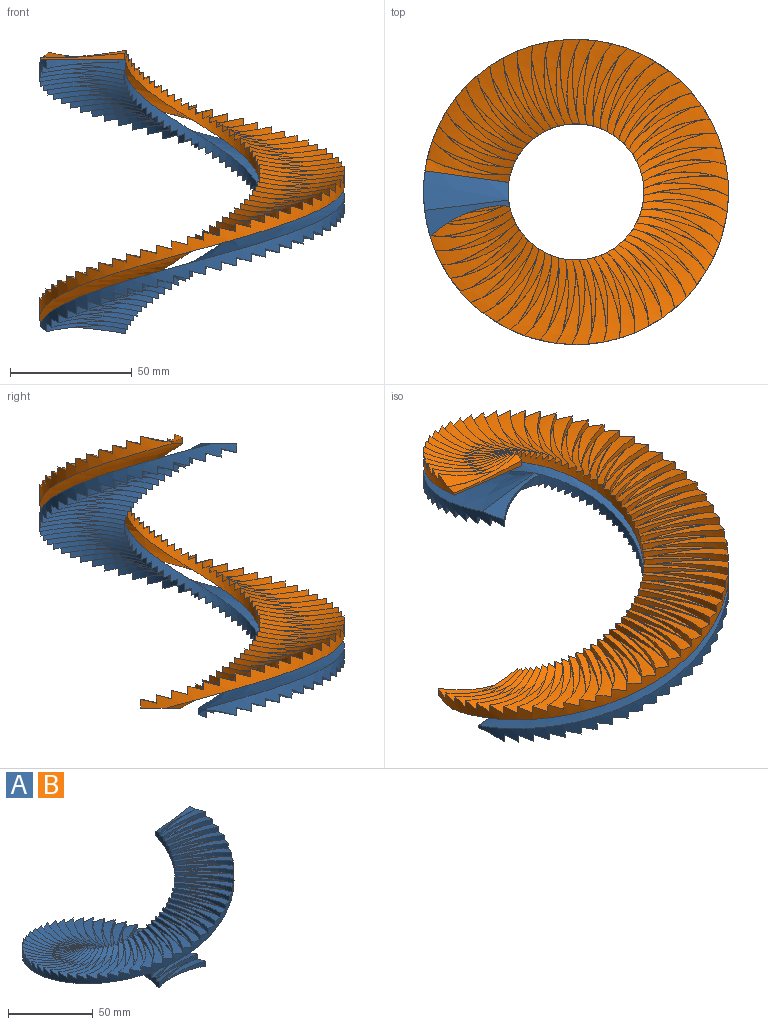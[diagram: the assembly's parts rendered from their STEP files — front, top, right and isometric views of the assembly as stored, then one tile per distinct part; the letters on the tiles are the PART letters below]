
ASSEMBLY  parts=2 mates=1
PART A: 249 faces, bbox 134.5x134.5x124.1 mm
  f0: cylinder r=27.93mm len=112.5mm, axis (0,0,-1), area 831.8mm2, adj f2,f3,f4,f5,f6,f7,f8,f9
  f1: cylinder r=62.62mm len=125.24mm, axis (0,0,-1), area 1964.2mm2, adj f2,f3,f4,f126,f127,f128,f129,f130
  f2: plane 34.97x10.85mm, normal (0,0,-1), area 146.9mm2, adj f0,f1,f125,f247,f248
  f3: plane 34.2x5.86mm, normal (-0.17,0.99,0), area 50.9mm2, adj f0,f1,f4,f248
  f4: bspline ~40.21x16.63mm, area 94.5mm2, adj f0,f1,f3,f5,f126
  f5: bspline ~39.85x15.98mm, area 49.6mm2, adj f0,f4,f6,f126
  f6: bspline ~38.72x13.77mm, area 65.8mm2, adj f0,f5,f7,f126,f127
  f7: bspline ~37.98x15.95mm, area 41.2mm2, adj f0,f6,f8,f127,f128,f129
  f8: bspline ~39.79x14.14mm, area 55mm2, adj f0,f7,f9,f129
  f9: bspline ~37.93x15.94mm, area 41.3mm2, adj f0,f8,f10,f129,f130,f131
  f10: bspline ~40.42x16.75mm, area 66.7mm2, adj f0,f9,f11,f131
  f11: bspline ~37.46x15.96mm, area 41.2mm2, adj f0,f10,f12,f131,f132,f133
  f12: bspline ~40.61x19.84mm, area 66.8mm2, adj f0,f11,f13,f133
  f13: bspline ~36.57x15.97mm, area 41.2mm2, adj f0,f12,f14,f133,f134,f135
  f14: bspline ~40.36x23.15mm, area 54.7mm2, adj f0,f13,f15,f135
  f15: bspline ~35.31x15.95mm, area 41.2mm2, adj f0,f14,f16,f135,f136,f137
  f16: bspline ~39.67x26.21mm, area 66.4mm2, adj f0,f15,f17,f137
  f17: bspline ~33.65x17.74mm, area 41.3mm2, adj f0,f16,f18,f137,f138,f139
  f18: bspline ~38.53x28.98mm, area 66.8mm2, adj f0,f17,f19,f139
  f19: bspline ~31.59x21.16mm, area 41.2mm2, adj f0,f18,f20,f139,f140,f141
  f20: bspline ~36.98x31.43mm, area 66.5mm2, adj f0,f19,f21,f141
  f21: bspline ~29.21x24.34mm, area 41.2mm2, adj f0,f20,f22,f141,f142,f143
  f22: bspline ~35.03x33.54mm, area 54.8mm2, adj f0,f21,f23,f143
  f23: bspline ~27.26x26.55mm, area 41.2mm2, adj f0,f22,f24,f143,f144,f145
  f24: bspline ~35.28x32.68mm, area 66.5mm2, adj f0,f23,f25,f145
  f25: bspline ~29.88x23.55mm, area 41.3mm2, adj f0,f24,f26,f145,f146,f147
  f26: bspline ~36.63x29.97mm, area 66.9mm2, adj f0,f25,f27,f147
  f27: bspline ~32.17x20.27mm, area 41.2mm2, adj f0,f26,f28,f147,f148,f149
  f28: bspline ~37.58x26.95mm, area 54.9mm2, adj f0,f27,f29,f149
  f29: bspline ~34.11x16.81mm, area 41.2mm2, adj f0,f28,f30,f149,f150,f151
  f30: bspline ~38.12x23.63mm, area 54.9mm2, adj f0,f29,f31,f151
  f31: bspline ~35.67x15.94mm, area 41.3mm2, adj f0,f30,f32,f151,f152,f153
  f32: bspline ~38.25x20.05mm, area 66.6mm2, adj f0,f31,f33,f153
  f33: bspline ~36.84x15.95mm, area 41.3mm2, adj f0,f32,f34,f153,f154,f155
  f34: bspline ~37.95x16.63mm, area 67.1mm2, adj f0,f33,f35,f155
  f35: bspline ~37.61x15.98mm, area 41.2mm2, adj f0,f34,f36,f155,f156
  f36: bspline ~38.72x13.77mm, area 65.8mm2, adj f0,f35,f37,f156,f157
  f37: bspline ~37.98x15.95mm, area 41.2mm2, adj f0,f36,f38,f157,f158,f159
  f38: bspline ~39.79x14.14mm, area 55mm2, adj f0,f37,f39,f159
  f39: bspline ~37.93x15.94mm, area 41.3mm2, adj f0,f38,f40,f159,f160,f161
  f40: bspline ~40.42x16.75mm, area 66.7mm2, adj f0,f39,f41,f161
  f41: bspline ~37.46x15.96mm, area 41.2mm2, adj f0,f40,f42,f161,f162,f163
  f42: bspline ~40.61x19.84mm, area 66.8mm2, adj f0,f41,f43,f163
  f43: bspline ~36.57x15.97mm, area 41.2mm2, adj f0,f42,f44,f163,f164,f165
  f44: bspline ~40.36x23.15mm, area 54.7mm2, adj f0,f43,f45,f165
  f45: bspline ~35.31x15.95mm, area 41.2mm2, adj f0,f44,f46,f165,f166,f167
  f46: bspline ~39.67x26.21mm, area 66.4mm2, adj f0,f45,f47,f167
  f47: bspline ~33.65x17.74mm, area 41.3mm2, adj f0,f46,f48,f167,f168,f169
  f48: bspline ~38.53x28.98mm, area 66.8mm2, adj f0,f47,f49,f169
  f49: bspline ~31.59x21.16mm, area 41.2mm2, adj f0,f48,f50,f169,f170,f171
  f50: bspline ~36.98x31.43mm, area 66.5mm2, adj f0,f49,f51,f171
  f51: bspline ~29.21x24.34mm, area 41.2mm2, adj f0,f50,f52,f171,f172,f173
  f52: bspline ~35.03x33.54mm, area 54.8mm2, adj f0,f51,f53,f173
  f53: bspline ~27.26x26.55mm, area 41.2mm2, adj f0,f52,f54,f173,f174,f175
  f54: bspline ~35.28x32.68mm, area 66.5mm2, adj f0,f53,f55,f175
  f55: bspline ~29.88x23.55mm, area 41.3mm2, adj f0,f54,f56,f175,f176,f177
  f56: bspline ~36.63x29.97mm, area 66.9mm2, adj f0,f55,f57,f177
  f57: bspline ~32.17x20.27mm, area 41.2mm2, adj f0,f56,f58,f177,f178,f179
  f58: bspline ~37.58x26.95mm, area 54.9mm2, adj f0,f57,f59,f179
  f59: bspline ~34.11x16.81mm, area 41.2mm2, adj f0,f58,f60,f179,f180,f181
  f60: bspline ~38.12x23.63mm, area 54.9mm2, adj f0,f59,f61,f181
  f61: bspline ~35.67x15.94mm, area 41.3mm2, adj f0,f60,f62,f181,f182,f183
  f62: bspline ~38.25x20.05mm, area 66.6mm2, adj f0,f61,f63,f183
  f63: bspline ~36.84x15.95mm, area 41.3mm2, adj f0,f62,f64,f183,f184,f185
  f64: bspline ~37.95x16.63mm, area 67.1mm2, adj f0,f63,f65,f185
  f65: bspline ~37.61x15.98mm, area 41.2mm2, adj f0,f64,f66,f185,f186
  f66: bspline ~38.72x13.77mm, area 65.8mm2, adj f0,f65,f67,f186,f187
  f67: bspline ~37.98x15.95mm, area 41.2mm2, adj f0,f66,f68,f187,f188,f189
  f68: bspline ~39.79x14.14mm, area 55mm2, adj f0,f67,f69,f189
  f69: bspline ~37.93x15.94mm, area 41.3mm2, adj f0,f68,f70,f189,f190,f191
  f70: bspline ~40.42x16.75mm, area 66.7mm2, adj f0,f69,f71,f191
  f71: bspline ~37.46x15.96mm, area 41.2mm2, adj f0,f70,f72,f191,f192,f193
  f72: bspline ~40.61x19.84mm, area 66.8mm2, adj f0,f71,f73,f193
  f73: bspline ~36.57x15.97mm, area 41.2mm2, adj f0,f72,f74,f193,f194,f195
  f74: bspline ~40.36x23.15mm, area 54.7mm2, adj f0,f73,f75,f195
  f75: bspline ~35.31x15.95mm, area 41.2mm2, adj f0,f74,f76,f195,f196,f197
  f76: bspline ~39.67x26.21mm, area 66.4mm2, adj f0,f75,f77,f197
  f77: bspline ~33.65x17.74mm, area 41.3mm2, adj f0,f76,f78,f197,f198,f199
  f78: bspline ~38.53x28.98mm, area 66.8mm2, adj f0,f77,f79,f199
  f79: bspline ~31.59x21.16mm, area 41.2mm2, adj f0,f78,f80,f199,f200,f201
  f80: bspline ~36.98x31.43mm, area 66.5mm2, adj f0,f79,f81,f201
  f81: bspline ~29.21x24.34mm, area 41.2mm2, adj f0,f80,f82,f201,f202,f203
  f82: bspline ~35.03x33.54mm, area 54.8mm2, adj f0,f81,f83,f203
  f83: bspline ~27.26x26.55mm, area 41.2mm2, adj f0,f82,f84,f203,f204,f205
  f84: bspline ~35.28x32.68mm, area 66.5mm2, adj f0,f83,f85,f205
  f85: bspline ~29.88x23.55mm, area 41.3mm2, adj f0,f84,f86,f205,f206,f207
  f86: bspline ~36.63x29.97mm, area 66.9mm2, adj f0,f85,f87,f207
  f87: bspline ~32.17x20.27mm, area 41.2mm2, adj f0,f86,f88,f207,f208,f209
  f88: bspline ~37.58x26.95mm, area 54.9mm2, adj f0,f87,f89,f209
  f89: bspline ~34.11x16.81mm, area 41.2mm2, adj f0,f88,f90,f209,f210,f211
  f90: bspline ~38.12x23.63mm, area 54.9mm2, adj f0,f89,f91,f211
  f91: bspline ~35.67x15.94mm, area 41.3mm2, adj f0,f90,f92,f211,f212,f213
  f92: bspline ~38.25x20.05mm, area 66.6mm2, adj f0,f91,f93,f213
  f93: bspline ~36.84x15.95mm, area 41.3mm2, adj f0,f92,f94,f213,f214,f215
  f94: bspline ~37.95x16.63mm, area 67.1mm2, adj f0,f93,f95,f215
  f95: bspline ~37.61x15.98mm, area 41.2mm2, adj f0,f94,f96,f215,f216
  f96: bspline ~38.72x13.77mm, area 65.8mm2, adj f0,f95,f97,f216,f217
  f97: bspline ~37.98x15.95mm, area 41.2mm2, adj f0,f96,f98,f217,f218,f219
  f98: bspline ~39.79x14.14mm, area 55mm2, adj f0,f97,f99,f219
  f99: bspline ~37.93x15.94mm, area 41.3mm2, adj f0,f98,f100,f219,f220,f221
  f100: bspline ~40.42x16.75mm, area 66.7mm2, adj f0,f99,f101,f221
  f101: bspline ~37.46x15.96mm, area 41.2mm2, adj f0,f100,f102,f221,f222,f223
  f102: bspline ~40.61x19.84mm, area 66.8mm2, adj f0,f101,f103,f223
  f103: bspline ~36.57x15.97mm, area 41.2mm2, adj f0,f102,f104,f223,f224,f225
  f104: bspline ~40.36x23.15mm, area 54.7mm2, adj f0,f103,f105,f225
  f105: bspline ~35.31x15.95mm, area 41.2mm2, adj f0,f104,f106,f225,f226,f227
  f106: bspline ~39.67x26.21mm, area 66.4mm2, adj f0,f105,f107,f227
  f107: bspline ~33.65x17.74mm, area 41.3mm2, adj f0,f106,f108,f227,f228,f229
  f108: bspline ~38.53x28.98mm, area 66.8mm2, adj f0,f107,f109,f229
  f109: bspline ~31.59x21.16mm, area 41.2mm2, adj f0,f108,f110,f229,f230,f231
  f110: bspline ~36.98x31.43mm, area 66.5mm2, adj f0,f109,f111,f231
  f111: bspline ~29.21x24.34mm, area 41.2mm2, adj f0,f110,f112,f231,f232,f233
  f112: bspline ~35.03x33.54mm, area 54.8mm2, adj f0,f111,f113,f233
  f113: bspline ~27.26x26.55mm, area 41.2mm2, adj f0,f112,f114,f233,f234,f235
  f114: bspline ~35.28x32.68mm, area 66.5mm2, adj f0,f113,f115,f235
  f115: bspline ~29.88x23.55mm, area 41.3mm2, adj f0,f114,f116,f235,f236,f237
  f116: bspline ~36.63x29.97mm, area 66.9mm2, adj f0,f115,f117,f237
  f117: bspline ~32.17x20.27mm, area 41.2mm2, adj f0,f116,f118,f237,f238,f239
  f118: bspline ~37.58x26.95mm, area 54.9mm2, adj f0,f117,f119,f239
  f119: bspline ~34.11x16.81mm, area 41.2mm2, adj f0,f118,f120,f239,f240,f241
  f120: bspline ~38.12x23.63mm, area 54.9mm2, adj f0,f119,f121,f241
  f121: bspline ~35.67x15.94mm, area 41.3mm2, adj f0,f120,f122,f241,f242,f243
  f122: bspline ~38.25x20.05mm, area 66.6mm2, adj f0,f121,f123,f243
  f123: bspline ~36.84x15.95mm, area 41.3mm2, adj f0,f122,f124,f243,f244,f245
  f124: bspline ~37.95x16.63mm, area 67.1mm2, adj f0,f123,f125,f245
  f125: bspline ~37.61x15.98mm, area 45.3mm2, adj f0,f2,f124,f245,f246,f247
  f126: bspline ~40.03x16.78mm, area 102.9mm2, adj f1,f4,f5,f6,f127
  f127: bspline ~39.98x15.05mm, area 56.2mm2, adj f1,f6,f7,f126,f128
  f128: bspline ~40.44x19.89mm, area 99.9mm2, adj f1,f7,f127,f129
  f129: bspline ~39.32x15.01mm, area 56.8mm2, adj f1,f7,f8,f9,f128,f130
  f130: bspline ~40.41x23.19mm, area 100mm2, adj f1,f9,f129,f131
  f131: bspline ~38.23x15mm, area 57.4mm2, adj f1,f9,f10,f11,f130,f132
  f132: bspline ~39.93x26.81mm, area 100mm2, adj f1,f11,f131,f133
  f133: bspline ~36.72x16.47mm, area 57.3mm2, adj f1,f11,f12,f13,f132,f134
  f134: bspline ~39.02x30.13mm, area 100.1mm2, adj f1,f13,f133,f135
  f135: bspline ~34.79x20.18mm, area 56.3mm2, adj f1,f13,f14,f15,f134,f136
  f136: bspline ~37.67x33.14mm, area 99.9mm2, adj f1,f15,f135,f137
  f137: bspline ~32.52x23.76mm, area 57mm2, adj f1,f15,f16,f17,f136,f138
  f138: bspline ~35.92x35.78mm, area 100mm2, adj f1,f17,f137,f139
  f139: bspline ~29.87x27.02mm, area 57.6mm2, adj f1,f17,f18,f19,f138,f140
  f140: bspline ~38.02x33.77mm, area 100.1mm2, adj f1,f19,f139,f141
  f141: bspline ~29.95x26.88mm, area 56.8mm2, adj f1,f19,f20,f21,f140,f142
  f142: bspline ~39.85x31.25mm, area 100mm2, adj f1,f21,f141,f143
  f143: bspline ~32.59x23.6mm, area 56.5mm2, adj f1,f21,f22,f23,f142,f144
  f144: bspline ~41.24x28.39mm, area 99.9mm2, adj f1,f23,f143,f145
  f145: bspline ~34.9x20.1mm, area 57.1mm2, adj f1,f23,f24,f25,f144,f146
  f146: bspline ~42.18x25.22mm, area 100mm2, adj f1,f25,f145,f147
  f147: bspline ~36.8x16.35mm, area 57.8mm2, adj f1,f25,f26,f27,f146,f148
  f148: bspline ~42.66x21.89mm, area 100.1mm2, adj f1,f27,f147,f149
  f149: bspline ~38.27x15.04mm, area 56.4mm2, adj f1,f27,f28,f29,f148,f150
  f150: bspline ~42.67x18.91mm, area 100mm2, adj f1,f29,f149,f151
  f151: bspline ~39.36x15.02mm, area 56.7mm2, adj f1,f29,f30,f31,f150,f152
  f152: bspline ~42.21x16.28mm, area 100mm2, adj f1,f31,f151,f153
  f153: bspline ~40.01x15mm, area 57.3mm2, adj f1,f31,f32,f33,f152,f154
  f154: bspline ~41.29x14.24mm, area 100mm2, adj f1,f33,f153,f155
  f155: bspline ~40.21x15.01mm, area 57.9mm2, adj f1,f33,f34,f35,f154,f156
  f156: bspline ~40.03x16.78mm, area 100.5mm2, adj f1,f35,f36,f155,f157
  f157: bspline ~39.98x15.05mm, area 56.2mm2, adj f1,f36,f37,f156,f158
  f158: bspline ~40.44x19.89mm, area 99.9mm2, adj f1,f37,f157,f159
  f159: bspline ~39.32x15.01mm, area 56.8mm2, adj f1,f37,f38,f39,f158,f160
  f160: bspline ~40.41x23.19mm, area 100mm2, adj f1,f39,f159,f161
  f161: bspline ~38.23x15mm, area 57.4mm2, adj f1,f39,f40,f41,f160,f162
  f162: bspline ~39.93x26.81mm, area 100mm2, adj f1,f41,f161,f163
  f163: bspline ~36.72x16.47mm, area 57.3mm2, adj f1,f41,f42,f43,f162,f164
  f164: bspline ~39.02x30.13mm, area 100.1mm2, adj f1,f43,f163,f165
  f165: bspline ~34.79x20.18mm, area 56.3mm2, adj f1,f43,f44,f45,f164,f166
  f166: bspline ~37.67x33.14mm, area 99.9mm2, adj f1,f45,f165,f167
  f167: bspline ~32.52x23.76mm, area 57mm2, adj f1,f45,f46,f47,f166,f168
  f168: bspline ~35.92x35.78mm, area 100mm2, adj f1,f47,f167,f169
  f169: bspline ~29.87x27.02mm, area 57.6mm2, adj f1,f47,f48,f49,f168,f170
  f170: bspline ~38.02x33.77mm, area 100.1mm2, adj f1,f49,f169,f171
  f171: bspline ~29.95x26.88mm, area 56.8mm2, adj f1,f49,f50,f51,f170,f172
  f172: bspline ~39.85x31.25mm, area 100mm2, adj f1,f51,f171,f173
  f173: bspline ~32.59x23.6mm, area 56.5mm2, adj f1,f51,f52,f53,f172,f174
  f174: bspline ~41.24x28.39mm, area 99.9mm2, adj f1,f53,f173,f175
  f175: bspline ~34.9x20.1mm, area 57.1mm2, adj f1,f53,f54,f55,f174,f176
  f176: bspline ~42.18x25.22mm, area 100mm2, adj f1,f55,f175,f177
  f177: bspline ~36.8x16.35mm, area 57.8mm2, adj f1,f55,f56,f57,f176,f178
  f178: bspline ~42.66x21.89mm, area 100.1mm2, adj f1,f57,f177,f179
  f179: bspline ~38.27x15.04mm, area 56.4mm2, adj f1,f57,f58,f59,f178,f180
  f180: bspline ~42.67x18.91mm, area 100mm2, adj f1,f59,f179,f181
  f181: bspline ~39.36x15.02mm, area 56.7mm2, adj f1,f59,f60,f61,f180,f182
  f182: bspline ~42.21x16.28mm, area 100mm2, adj f1,f61,f181,f183
  f183: bspline ~40.01x15mm, area 57.3mm2, adj f1,f61,f62,f63,f182,f184
  f184: bspline ~41.29x14.24mm, area 100mm2, adj f1,f63,f183,f185
  f185: bspline ~40.21x15.01mm, area 57.9mm2, adj f1,f63,f64,f65,f184,f186
  f186: bspline ~40.03x16.78mm, area 100.5mm2, adj f1,f65,f66,f185,f187
  f187: bspline ~39.98x15.05mm, area 56.2mm2, adj f1,f66,f67,f186,f188
  f188: bspline ~40.44x19.89mm, area 99.9mm2, adj f1,f67,f187,f189
  f189: bspline ~39.32x15.01mm, area 56.8mm2, adj f1,f67,f68,f69,f188,f190
  f190: bspline ~40.41x23.19mm, area 100mm2, adj f1,f69,f189,f191
  f191: bspline ~38.23x15mm, area 57.4mm2, adj f1,f69,f70,f71,f190,f192
  f192: bspline ~39.93x26.81mm, area 100mm2, adj f1,f71,f191,f193
  f193: bspline ~36.72x16.47mm, area 57.3mm2, adj f1,f71,f72,f73,f192,f194
  f194: bspline ~39.02x30.13mm, area 100.1mm2, adj f1,f73,f193,f195
  f195: bspline ~34.79x20.18mm, area 56.3mm2, adj f1,f73,f74,f75,f194,f196
  f196: bspline ~37.67x33.14mm, area 99.9mm2, adj f1,f75,f195,f197
  f197: bspline ~32.52x23.76mm, area 57mm2, adj f1,f75,f76,f77,f196,f198
  f198: bspline ~35.92x35.78mm, area 100mm2, adj f1,f77,f197,f199
  f199: bspline ~29.87x27.02mm, area 57.6mm2, adj f1,f77,f78,f79,f198,f200
  f200: bspline ~38.02x33.77mm, area 100.1mm2, adj f1,f79,f199,f201
  f201: bspline ~29.95x26.88mm, area 56.8mm2, adj f1,f79,f80,f81,f200,f202
  f202: bspline ~39.85x31.25mm, area 100mm2, adj f1,f81,f201,f203
  f203: bspline ~32.59x23.6mm, area 56.5mm2, adj f1,f81,f82,f83,f202,f204
  f204: bspline ~41.24x28.39mm, area 99.9mm2, adj f1,f83,f203,f205
  f205: bspline ~34.9x20.1mm, area 57.1mm2, adj f1,f83,f84,f85,f204,f206
  f206: bspline ~42.18x25.22mm, area 100mm2, adj f1,f85,f205,f207
  f207: bspline ~36.8x16.35mm, area 57.8mm2, adj f1,f85,f86,f87,f206,f208
  f208: bspline ~42.66x21.89mm, area 100.1mm2, adj f1,f87,f207,f209
  f209: bspline ~38.27x15.04mm, area 56.4mm2, adj f1,f87,f88,f89,f208,f210
  f210: bspline ~42.67x18.91mm, area 100mm2, adj f1,f89,f209,f211
  f211: bspline ~39.36x15.02mm, area 56.7mm2, adj f1,f89,f90,f91,f210,f212
  f212: bspline ~42.21x16.28mm, area 100mm2, adj f1,f91,f211,f213
  f213: bspline ~40.01x15mm, area 57.3mm2, adj f1,f91,f92,f93,f212,f214
  f214: bspline ~41.29x14.24mm, area 100mm2, adj f1,f93,f213,f215
  f215: bspline ~40.21x15.01mm, area 57.9mm2, adj f1,f93,f94,f95,f214,f216
  f216: bspline ~40.03x16.78mm, area 100.5mm2, adj f1,f95,f96,f215,f217
  f217: bspline ~39.98x15.05mm, area 56.2mm2, adj f1,f96,f97,f216,f218
  f218: bspline ~40.44x19.89mm, area 99.9mm2, adj f1,f97,f217,f219
  f219: bspline ~39.32x15.01mm, area 56.8mm2, adj f1,f97,f98,f99,f218,f220
  f220: bspline ~40.41x23.19mm, area 100mm2, adj f1,f99,f219,f221
  f221: bspline ~38.23x15mm, area 57.4mm2, adj f1,f99,f100,f101,f220,f222
  f222: bspline ~39.93x26.81mm, area 100mm2, adj f1,f101,f221,f223
  f223: bspline ~36.72x16.47mm, area 57.3mm2, adj f1,f101,f102,f103,f222,f224
  f224: bspline ~39.02x30.13mm, area 100.1mm2, adj f1,f103,f223,f225
  f225: bspline ~34.79x20.18mm, area 56.3mm2, adj f1,f103,f104,f105,f224,f226
  f226: bspline ~37.67x33.14mm, area 99.9mm2, adj f1,f105,f225,f227
  f227: bspline ~32.52x23.76mm, area 57mm2, adj f1,f105,f106,f107,f226,f228
  f228: bspline ~35.92x35.78mm, area 100mm2, adj f1,f107,f227,f229
  f229: bspline ~29.87x27.02mm, area 57.6mm2, adj f1,f107,f108,f109,f228,f230
  f230: bspline ~38.02x33.77mm, area 100.1mm2, adj f1,f109,f229,f231
  f231: bspline ~29.95x26.88mm, area 56.8mm2, adj f1,f109,f110,f111,f230,f232
  f232: bspline ~39.85x31.25mm, area 100mm2, adj f1,f111,f231,f233
  f233: bspline ~32.59x23.6mm, area 56.5mm2, adj f1,f111,f112,f113,f232,f234
  f234: bspline ~41.24x28.39mm, area 99.9mm2, adj f1,f113,f233,f235
  f235: bspline ~34.9x20.1mm, area 57.1mm2, adj f1,f113,f114,f115,f234,f236
  f236: bspline ~42.18x25.22mm, area 100mm2, adj f1,f115,f235,f237
  f237: bspline ~36.8x16.35mm, area 57.8mm2, adj f1,f115,f116,f117,f236,f238
  f238: bspline ~42.66x21.89mm, area 100.1mm2, adj f1,f117,f237,f239
  f239: bspline ~38.27x15.04mm, area 56.4mm2, adj f1,f117,f118,f119,f238,f240
  f240: bspline ~42.67x18.91mm, area 100mm2, adj f1,f119,f239,f241
  f241: bspline ~39.36x15.02mm, area 56.7mm2, adj f1,f119,f120,f121,f240,f242
  f242: bspline ~42.21x16.28mm, area 100mm2, adj f1,f121,f241,f243
  f243: bspline ~40.01x15mm, area 57.3mm2, adj f1,f121,f122,f123,f242,f244
  f244: bspline ~41.29x14.24mm, area 100mm2, adj f1,f123,f243,f245
  f245: bspline ~40.21x15.01mm, area 57.9mm2, adj f1,f123,f124,f125,f244,f246
  f246: bspline ~40.03x16.78mm, area 100.1mm2, adj f1,f125,f245,f247
  f247: bspline ~39.98x15.05mm, area 61.2mm2, adj f1,f2,f125,f246
  f248: bspline ~134.46x134.46mm, area 10637.6mm2, adj f0,f1,f2,f3
PART B: same geometry as A
PLACE A rot(axis=(-0.13,0.99,0),180deg) t=(-8.07,-0.24,62.63)mm
PLACE B rot(axis=(0,0,1),162.4deg) t=(-8.07,-0.24,126.32)mm
MATE cylindrical A.f1 <-> B.f1  axis (0,0,1) through (-8.07,-0.24,92.59)mm
